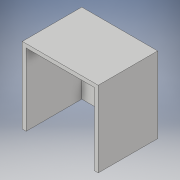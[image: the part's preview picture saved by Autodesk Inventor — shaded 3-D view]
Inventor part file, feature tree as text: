
AUTODESK INVENTOR PART (.ipt)
format: ipt  version: 2018 (Build 220112000, 112)  size: 124,416 bytes
history: native  units: mm
features: extrude x3, sketch x3
ambient origin geometry x8: Origin, YZ Plane, XZ Plane, XY Plane, X Axis, Y Axis, Z Axis, Center Point
bodies: Volumenkörper1 (feature_tree)
feature tree (6):
  extrude  "Extrusion1"  Depth=22.0mm TaperAngle=0.0deg
  extrude  "Extrusion2"  Depth=1.5mm
  extrude  "Extrusion4"  Depth=1.5mm
  sketch  "Skizze1"  dims[d3=22.0mm d4=0.0mm d5=22.0mm d6=0.0mm]
  sketch  "Skizze2"  dims[d7=28.2mm d8=1.5mm]
  sketch  "Skizze5"  dims[d9=1.5mm d10=1.5mm d17=2.7mm d18=1.5mm d19=0.0mm d20=30.0mm d21=30.0mm]
